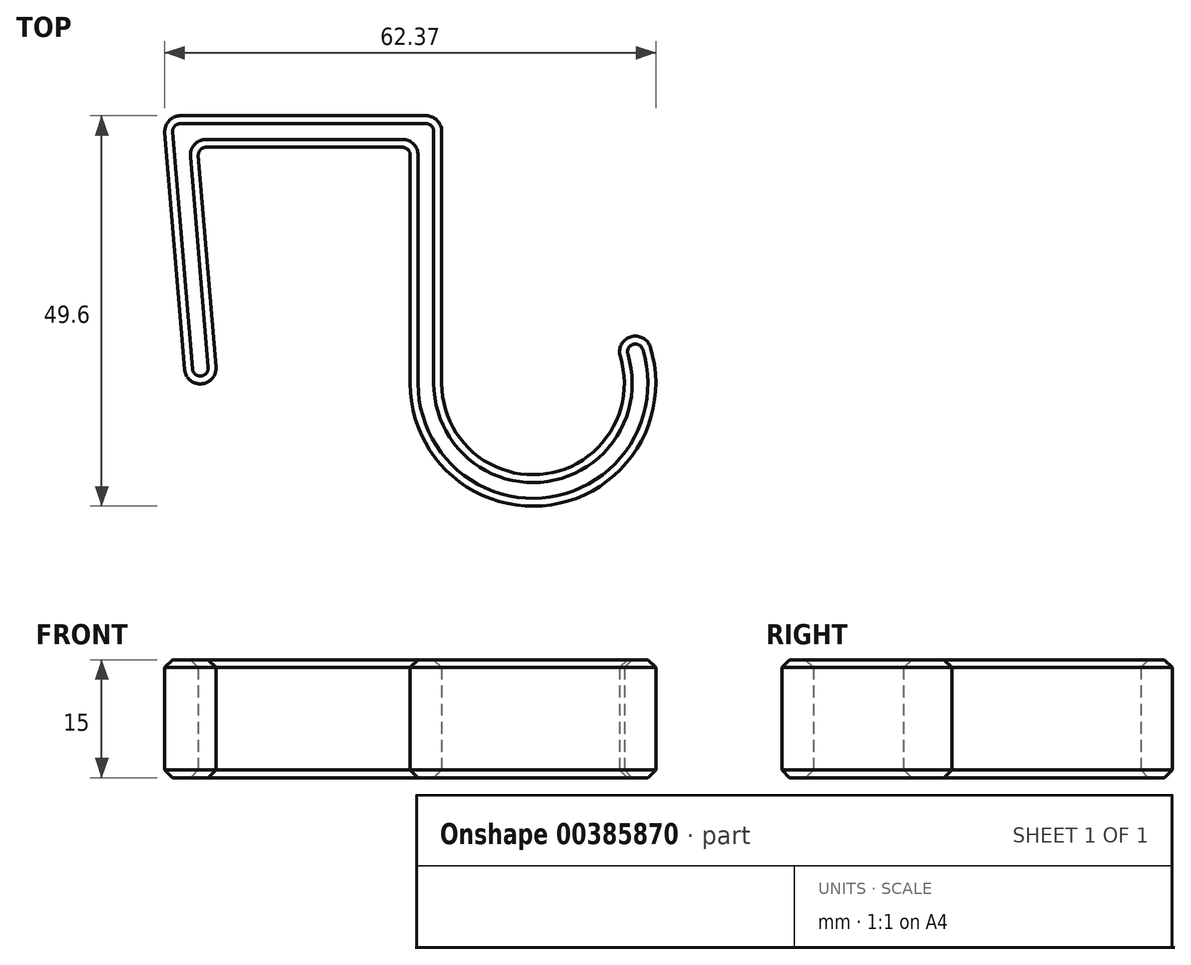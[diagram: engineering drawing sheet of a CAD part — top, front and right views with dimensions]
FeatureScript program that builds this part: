
annotation { "Feature Type Name" : "Feature", "Feature Type Description" : "" }
export const myFeature = defineFeature(function(context is Context, id is Id, definition is map)
    precondition{}
    {
        {
            var Q0;
            Q0=qCreatedBy(makeId("Top.planeOp"),FACE);
            var sketch = newSketch(context, id + "F0", { "sketchPlane" : qUnion([Q0])});
            skLineSegment(sketch, "E0", {"start": v(0, 0) * mm, "end": v(27, 0) * mm});
            skLineSegment(sketch, "E1", {"start": v(27, 0) * mm, "end": v(27, -30) * mm});
            skLineSegment(sketch, "E2", {"start": v(0, 0) * mm, "end": v(2.5, -29.9) * mm});
            skArc(sketch, "E3", {"start": v(27, -30) * mm, "mid": v(45.66, -45.3) * mm, "end": v(57, -24) * mm});
            skLineSegment(sketch, "E4.0", {"start": v(-4.35, 4) * mm, "end": v(-1.49, -30.23) * mm});
            skLineSegment(sketch, "E4.1", {"start": v(-4.35, 4) * mm, "end": v(31, 4) * mm});
            skLineSegment(sketch, "E4.2", {"start": v(31, 4) * mm, "end": v(31, -30) * mm});
            skArc(sketch, "E4.3", {"start": v(31, -30) * mm, "mid": v(45.71, -41.17) * mm, "end": v(52.53, -24) * mm});
            skLineSegment(sketch, "E5", {"start": v(-1.49, -30.23) * mm, "end": v(2.5, -29.9) * mm});
            skLineSegment(sketch, "E6", {"start": v(52.53, -24) * mm, "end": v(57, -24) * mm});
            skSolve(sketch);
        }
        {
            var Q0;
            Q0=makeQuery(id+"F0.imprint","IMPRINT",FACE,{"disambiguationData":[TD([[makeQuery(id+"F0.imprint","IMPRINT",EDGE,{"derivedFrom":sQuery(id+"F0.wireOp",EDGE,"E0")}),1.0]])]});
            extrude(context, id + "F1", {"entities" : qUnion([Q0]), "depth" : 15 * mm});
        }
        {
            var Q0;
            Q0=makeQuery(id+"F1.opExtrude","SWEPT_EDGE",EDGE,{"disambiguationData":[OSD([sQuery(id+"F0.wireOp",EDGE,"E2"),sQuery(id+"F0.wireOp",EDGE,"E5")])]});
            var Q1;
            Q1=makeQuery(id+"F1.opExtrude","SWEPT_EDGE",EDGE,{"disambiguationData":[OSD([sQuery(id+"F0.wireOp",EDGE,"E4.0"),sQuery(id+"F0.wireOp",EDGE,"E5")])]});
            var Q2;
            Q2=makeQuery(id+"F1.opExtrude","SWEPT_EDGE",EDGE,{"disambiguationData":[OSD([sQuery(id+"F0.wireOp",EDGE,"E4.3"),sQuery(id+"F0.wireOp",EDGE,"E6")])]});
            var Q3;
            Q3=makeQuery(id+"F1.opExtrude","SWEPT_EDGE",EDGE,{"disambiguationData":[OSD([sQuery(id+"F0.wireOp",EDGE,"E3"),sQuery(id+"F0.wireOp",EDGE,"E6")])]});
            fillet(context, id + "F2", {"entities" : qUnion([Q0, Q1, Q2, Q3]), "radius" : 2 * mm, "tangentPropagation" : true, "allowEdgeOverflow" : false});
        }
        {
            var Q0;
            Q0=makeQuery(id+"F1.opExtrude","SWEPT_EDGE",EDGE,{"disambiguationData":[OSD([sQuery(id+"F0.wireOp",EDGE,"E4.1"),sQuery(id+"F0.wireOp",EDGE,"E4.2")])]});
            var Q1;
            Q1=makeQuery(id+"F1.opExtrude","SWEPT_EDGE",EDGE,{"disambiguationData":[OSD([sQuery(id+"F0.wireOp",EDGE,"E4.0"),sQuery(id+"F0.wireOp",EDGE,"E4.1")])]});
            fillet(context, id + "F3", {"entities" : qUnion([Q0, Q1]), "radius" : 2 * mm, "tangentPropagation" : true, "allowEdgeOverflow" : false});
        }
        {
            var Q0;
            Q0=makeQuery(id+"F1.opExtrude","SWEPT_EDGE",EDGE,{"disambiguationData":[OSD([sQuery(id+"F0.wireOp",EDGE,"E0"),sQuery(id+"F0.wireOp",EDGE,"E2")])]});
            var Q1;
            Q1=makeQuery(id+"F1.opExtrude","SWEPT_EDGE",EDGE,{"disambiguationData":[OSD([sQuery(id+"F0.wireOp",EDGE,"E0"),sQuery(id+"F0.wireOp",EDGE,"E1")])]});
            fillet(context, id + "F4", {"entities" : qUnion([Q0, Q1]), "radius" : 1 * mm, "tangentPropagation" : true, "allowEdgeOverflow" : false});
        }
        {
            var Q0;
            Q0=makeQuery(id+"F1.opExtrude","CAP_FACE",FACE,{"disambiguationData":[OSD([sQuery(id+"F0.wireOp",EDGE,"E0"),sQuery(id+"F0.wireOp",EDGE,"E1"),sQuery(id+"F0.wireOp",EDGE,"E2"),sQuery(id+"F0.wireOp",EDGE,"E3"),sQuery(id+"F0.wireOp",EDGE,"E4.0"),sQuery(id+"F0.wireOp",EDGE,"E4.1"),sQuery(id+"F0.wireOp",EDGE,"E4.2"),sQuery(id+"F0.wireOp",EDGE,"E4.3"),sQuery(id+"F0.wireOp",EDGE,"E5"),sQuery(id+"F0.wireOp",EDGE,"E6")])],"isStart":false});
            var Q1;
            Q1=makeQuery(id+"F1.opExtrude","CAP_FACE",FACE,{"disambiguationData":[OSD([sQuery(id+"F0.wireOp",EDGE,"E0"),sQuery(id+"F0.wireOp",EDGE,"E1"),sQuery(id+"F0.wireOp",EDGE,"E2"),sQuery(id+"F0.wireOp",EDGE,"E3"),sQuery(id+"F0.wireOp",EDGE,"E4.0"),sQuery(id+"F0.wireOp",EDGE,"E4.1"),sQuery(id+"F0.wireOp",EDGE,"E4.2"),sQuery(id+"F0.wireOp",EDGE,"E4.3"),sQuery(id+"F0.wireOp",EDGE,"E5"),sQuery(id+"F0.wireOp",EDGE,"E6")])],"isStart":true});
            chamfer(context, id + "F5", {"entities" : qUnion([Q0, Q1]), "width" : 1 * mm, "tangentPropagation" : true});
        }
    });
